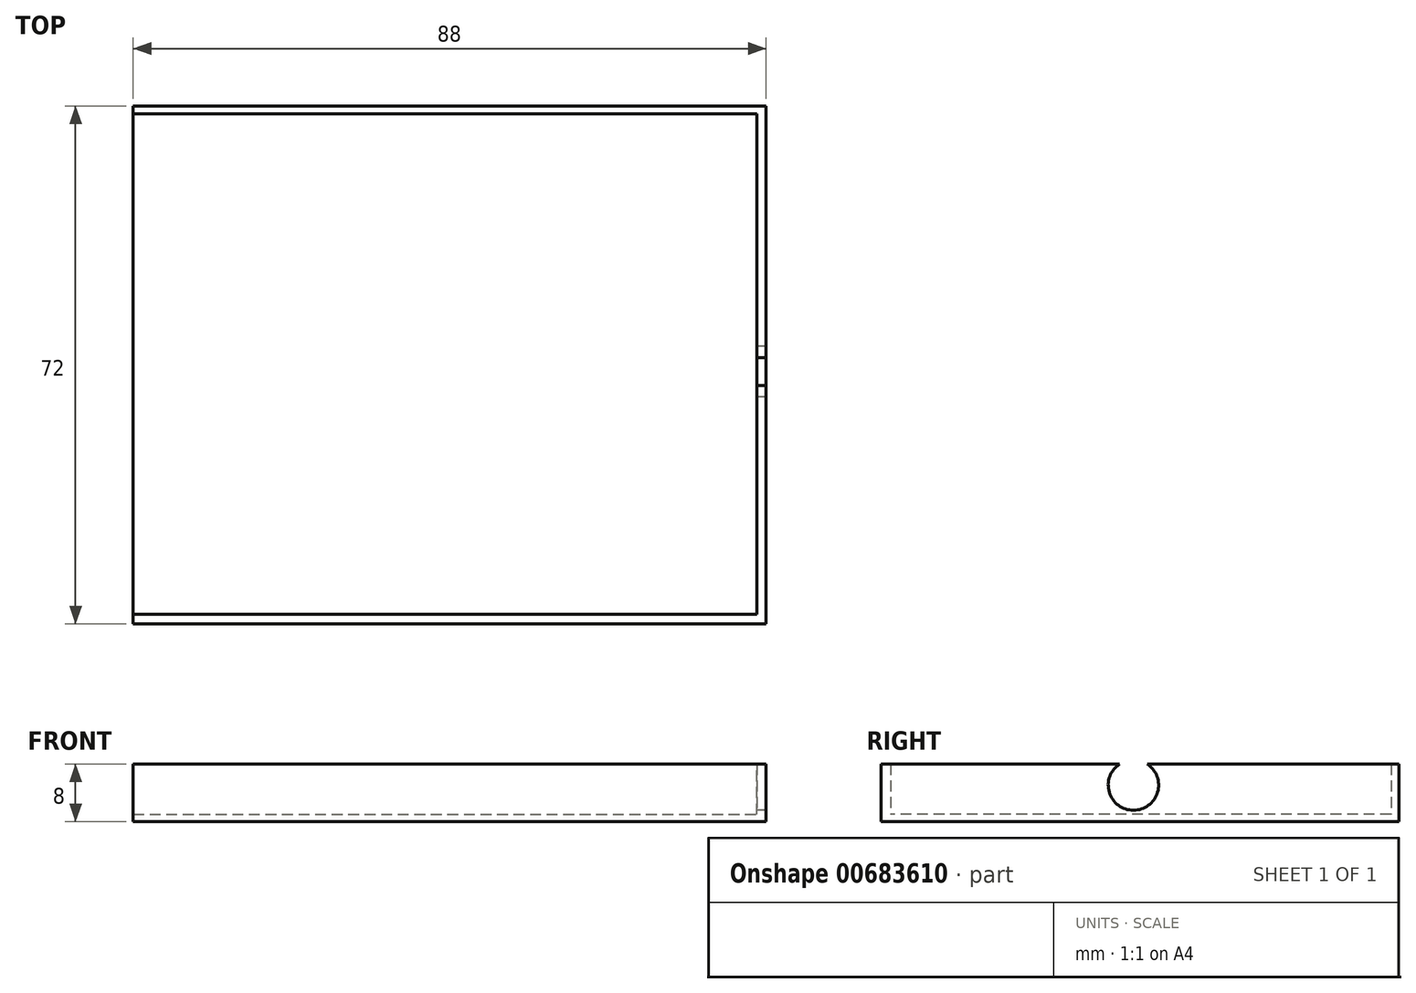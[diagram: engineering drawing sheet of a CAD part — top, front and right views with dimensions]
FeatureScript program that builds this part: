
annotation { "Feature Type Name" : "Feature", "Feature Type Description" : "" }
export const myFeature = defineFeature(function(context is Context, id is Id, definition is map)
    precondition{}
    {
        {
            var Q0;
            Q0=qCreatedBy(makeId("Top.planeOp"),FACE);
            var sketch = newSketch(context, id + "F0", { "sketchPlane" : qUnion([Q0])});
            skLineSegment(sketch, "E0.bottom", {"start": v(-46.6, 36.92) * mm, "end": v(43.4, 36.92) * mm});
            skLineSegment(sketch, "E0.top", {"start": v(-46.6, -35.08) * mm, "end": v(43.4, -35.08) * mm});
            skLineSegment(sketch, "E0.left", {"start": v(-46.6, 36.92) * mm, "end": v(-46.6, -35.08) * mm});
            skLineSegment(sketch, "E0.right", {"start": v(43.4, 36.92) * mm, "end": v(43.4, -35.08) * mm});
            skSolve(sketch);
        }
        {
            var Q0;
            Q0=makeQuery(id+"F0.imprint","IMPRINT",FACE,{"disambiguationData":[TD([[makeQuery(id+"F0.imprint","IMPRINT",EDGE,{"derivedFrom":sQuery(id+"F0.wireOp",EDGE,"E0.bottom")}),-1.0]])]});
            extrude(context, id + "F1", {"entities" : qUnion([Q0]), "depth" : 8 * mm, "offsetDistance" : 25 * mm});
        }
        {
            var Q0;
            Q0=makeQuery(id+"F1.opExtrude","CAP_FACE",FACE,{"disambiguationData":[OSD([sQuery(id+"F0.wireOp",EDGE,"E0.bottom"),sQuery(id+"F0.wireOp",EDGE,"E0.top"),sQuery(id+"F0.wireOp",EDGE,"E0.left"),sQuery(id+"F0.wireOp",EDGE,"E0.right")])],"isStart":false});
            var sketch = newSketch(context, id + "F2", { "sketchPlane" : qUnion([Q0])});
            skLineSegment(sketch, "E1", {"start": v(-43.2, 36.92) * mm, "end": v(-43.2, 35.92) * mm});
            skLineSegment(sketch, "E2", {"start": v(-43.49, -35.08) * mm, "end": v(-43.49, -34.08) * mm});
            skLineSegment(sketch, "E3", {"start": v(-46.6, 32.9) * mm, "end": v(-45.6, 32.9) * mm});
            skLineSegment(sketch, "E4.bottom", {"start": v(-45.48, 35.82) * mm, "end": v(42.1, 35.82) * mm});
            skLineSegment(sketch, "E4.top", {"start": v(-45.48, -33.73) * mm, "end": v(42.1, -33.73) * mm});
            skLineSegment(sketch, "E4.left", {"start": v(-45.48, 35.82) * mm, "end": v(-45.48, -33.73) * mm});
            skLineSegment(sketch, "E4.right", {"start": v(42.1, 35.82) * mm, "end": v(42.1, -33.73) * mm});
            skSolve(sketch);
        }
        {
            var Q0;
            Q0 = qSketchRegion(id + "F2", true);
            extrude(context, id + "F3", {"entities" : qUnion([Q0]), "operationType" : NewBodyOperationType.REMOVE, "depth" : -7 * mm, "offsetDistance" : 25 * mm});
        }
        {
            var Q0;
            Q0=makeQuery(id+"F1.opExtrude","SWEPT_FACE",FACE,{"disambiguationData":[OSD([sQuery(id+"F0.wireOp",EDGE,"E0.left")])]});
            var sketch = newSketch(context, id + "F4", { "sketchPlane" : qUnion([Q0])});
            skLineSegment(sketch, "E5", {"start": v(-36.92, 4) * mm, "end": v(0, 5.07) * mm});
            skSolve(sketch);
        }
        {
            var Q0;
            Q0=sQuery(id+"F4.wireOp",VERTEX,"E5.end");
            var Q1;
            Q1=makeQuery(id+"F1.opExtrude","SWEPT_BODY",BODY,{"disambiguationData":[OSD([sQuery(id+"F0.wireOp",EDGE,"E0.bottom"),sQuery(id+"F0.wireOp",EDGE,"E0.top"),sQuery(id+"F0.wireOp",EDGE,"E0.left"),sQuery(id+"F0.wireOp",EDGE,"E0.right")])]});
            hole(context, id + "F5", {"style" : HoleStyle.C_BORE, "endStyle" : HoleEndStyle.THROUGH, "holeDiameter" : 7 * mm, "cBoreDiameter" : 7 * mm, "cBoreDepth" : 1 * mm, "majorDiameter" : 5 * mm, "isTappedThrough" : true, "tappedDepth" : 12 * mm, "tapClearance" : 3, "locations" : qUnion([Q0]), "scope" : qUnion([Q1])});
        }
        {
            var Q0;
            Q0=makeQuery(id+"F1.opExtrude","SWEPT_FACE",FACE,{"disambiguationData":[OSD([sQuery(id+"F0.wireOp",EDGE,"E0.left")])]});
            var sketch = newSketch(context, id + "F6", { "sketchPlane" : qUnion([Q0])});
            skSolve(sketch);
        }
        {
            var Q0;
            {var subQ1=sQuery(id+"F0.wireOp",EDGE,"E0.left");Q0=makeQuery(id+"F6.imprint","IMPRINT",FACE,{"disambiguationData":[TD([[makeQuery(id+"F6.imprint","IMPRINT",EDGE,{"derivedFrom":makeQuery(id+"F1.opExtrude","CAP_EDGE",EDGE,{"disambiguationData":[OSD([subQ1])],"isStart":true})}),1.0]])]});}
            extrude(context, id + "F7", {"entities" : qUnion([Q0]), "operationType" : NewBodyOperationType.REMOVE, "oppositeDirection" : true, "depth" : 2 * mm, "offsetDistance" : 25 * mm});
        }
    });
